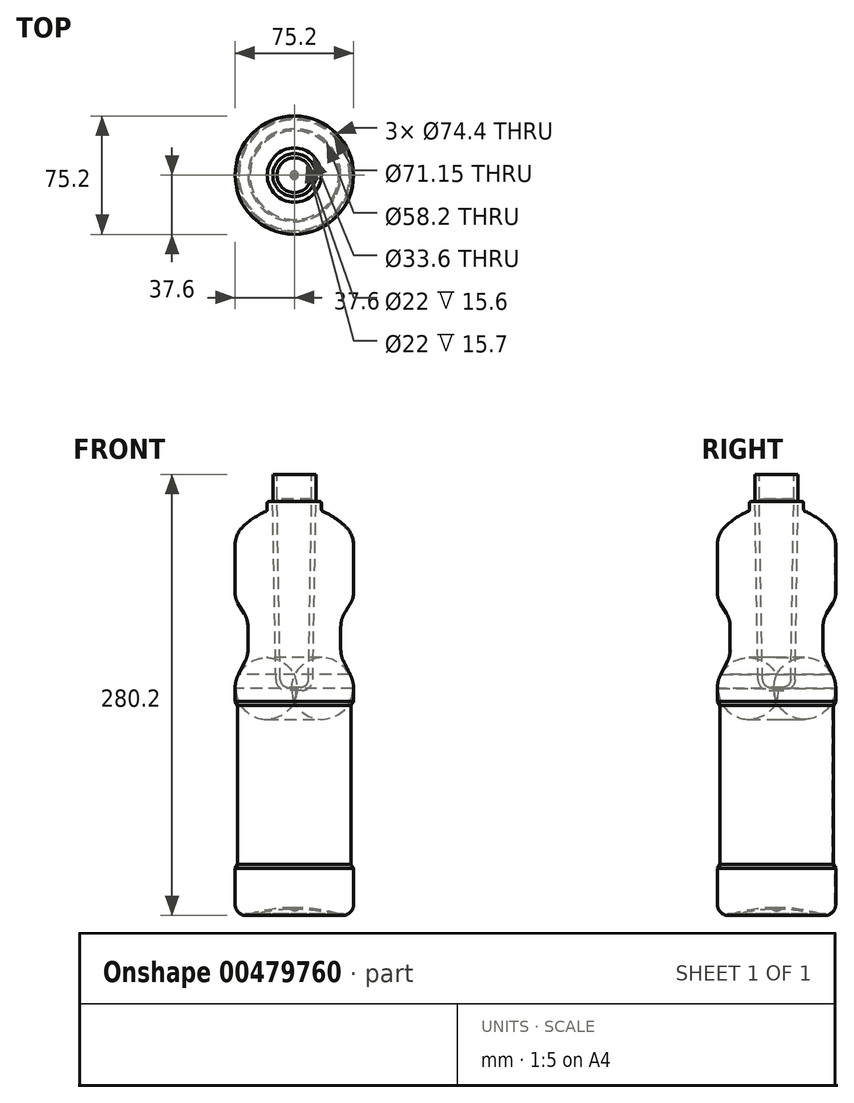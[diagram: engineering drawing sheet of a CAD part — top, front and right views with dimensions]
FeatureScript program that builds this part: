
annotation { "Feature Type Name" : "Feature", "Feature Type Description" : "" }
export const myFeature = defineFeature(function(context is Context, id is Id, definition is map)
    precondition{}
    {
        {
            var Q0;
            Q0=qCreatedBy(makeId("Front.planeOp"),FACE);
            var sketch = newSketch(context, id + "F0", { "sketchPlane" : qUnion([Q0])});
            skLineSegment(sketch, "E0", {"start": v(7.8, 140.1) * mm, "end": v(5.15, 140.1) * mm});
            skLineSegment(sketch, "E1", {"start": v(-11.8, -140.1) * mm, "end": v(-9.3, -140.1) * mm});
            skArc(sketch, "E2", {"start": v(16.2, -136.13) * mm, "mid": v(3.32, -137.3) * mm, "end": v(-9.3, -140.1) * mm});
            skLineSegment(sketch, "E3", {"start": v(-18.8, -133.1) * mm, "end": v(-18.8, -110.1) * mm});
            skArc(sketch, "E4", {"start": v(-18.8, -133.1) * mm, "mid": v(-16.75, -138.05) * mm, "end": v(-11.8, -140.1) * mm});
            skLineSegment(sketch, "E5", {"start": v(-17.18, -107.6) * mm, "end": v(-18.8, -110.1) * mm});
            skLineSegment(sketch, "E6", {"start": v(-17.18, -6.6) * mm, "end": v(-17.18, -107.6) * mm});
            skLineSegment(sketch, "E7", {"start": v(-17.18, -6.6) * mm, "end": v(-18.8, -4.1) * mm});
            skLineSegment(sketch, "E8", {"start": v(-16.64, 13.16) * mm, "end": v(-12.43, 21.5) * mm});
            skLineSegment(sketch, "E9", {"start": v(-10.7, 28.72) * mm, "end": v(-10.7, 43.47) * mm});
            skLineSegment(sketch, "E10", {"start": v(-12.98, 51.7) * mm, "end": v(-17.09, 58.55) * mm});
            skArc(sketch, "E11", {"start": v(-16.64, 13.16) * mm, "mid": v(-18.25, 8.77) * mm, "end": v(-18.8, 4.13) * mm});
            skArc(sketch, "E12", {"start": v(-12.43, 21.5) * mm, "mid": v(-11.14, 25) * mm, "end": v(-10.7, 28.72) * mm});
            skArc(sketch, "E13", {"start": v(-10.7, 43.47) * mm, "mid": v(-11.28, 47.74) * mm, "end": v(-12.98, 51.7) * mm});
            skLineSegment(sketch, "E14", {"start": v(-18.8, 64.72) * mm, "end": v(-18.8, 95.32) * mm});
            skArc(sketch, "E15", {"start": v(-18.8, 64.72) * mm, "mid": v(-18.36, 61.52) * mm, "end": v(-17.09, 58.55) * mm});
            skArc(sketch, "E16", {"start": v(-14.11, 106.63) * mm, "mid": v(-17.58, 101.44) * mm, "end": v(-18.8, 95.32) * mm});
            skArc(sketch, "E17", {"start": v(0.68, 116.6) * mm, "mid": v(-7.2, 112.33) * mm, "end": v(-14.11, 106.63) * mm});
            skLineSegment(sketch, "E18", {"start": v(-18.8, -4.1) * mm, "end": v(-18.8, 4.13) * mm});
            skLineSegment(sketch, "E19", {"start": v(5.15, 123.9) * mm, "end": v(5.15, 140.1) * mm});
            skLineSegment(sketch, "E20", {"start": v(1.6, 117.98) * mm, "end": v(1.6, 121.9) * mm});
            skLineSegment(sketch, "E21", {"start": v(2.6, 122.9) * mm, "end": v(4.15, 122.9) * mm});
            skLineSegment(sketch, "E22", {"start": v(7.8, 140.1) * mm, "end": v(7.8, 124.4) * mm});
            skArc(sketch, "E23", {"start": v(2.6, 122.9) * mm, "mid": v(1.9, 122.6) * mm, "end": v(1.6, 121.9) * mm});
            skArc(sketch, "E24", {"start": v(4.15, 122.9) * mm, "mid": v(4.85, 123.2) * mm, "end": v(5.15, 123.9) * mm});
            skArc(sketch, "E25", {"start": v(0.68, 116.6) * mm, "mid": v(1.35, 117.15) * mm, "end": v(1.6, 117.98) * mm});
            skArc(sketch, "E26", {"start": v(0.88, 116.13) * mm, "mid": v(-6.92, 111.91) * mm, "end": v(-13.76, 106.28) * mm});
            skArc(sketch, "E27", {"start": v(-13.76, 106.28) * mm, "mid": v(-17.12, 101.25) * mm, "end": v(-18.3, 95.32) * mm});
            skLineSegment(sketch, "E28", {"start": v(-18.3, 64.72) * mm, "end": v(-18.3, 95.32) * mm});
            skArc(sketch, "E29", {"start": v(-18.3, 64.72) * mm, "mid": v(-17.88, 61.65) * mm, "end": v(-16.66, 58.8) * mm});
            skLineSegment(sketch, "E30", {"start": v(-12.55, 51.96) * mm, "end": v(-16.66, 58.8) * mm});
            skArc(sketch, "E31", {"start": v(-10.2, 43.47) * mm, "mid": v(-10.8, 47.87) * mm, "end": v(-12.55, 51.96) * mm});
            skLineSegment(sketch, "E32", {"start": v(-10.2, 28.72) * mm, "end": v(-10.2, 43.47) * mm});
            skArc(sketch, "E33", {"start": v(-11.98, 21.27) * mm, "mid": v(-10.65, 24.89) * mm, "end": v(-10.2, 28.72) * mm});
            skLineSegment(sketch, "E34", {"start": v(-16.2, 12.93) * mm, "end": v(-11.98, 21.27) * mm});
            skArc(sketch, "E35", {"start": v(-16.2, 12.93) * mm, "mid": v(-17.77, 8.65) * mm, "end": v(-18.3, 4.13) * mm});
            skLineSegment(sketch, "E36", {"start": v(-18.3, -3.95) * mm, "end": v(-18.3, 4.13) * mm});
            skLineSegment(sketch, "E37", {"start": v(-16.68, -6.45) * mm, "end": v(-18.3, -3.95) * mm});
            skLineSegment(sketch, "E38", {"start": v(-16.68, -6.45) * mm, "end": v(-16.68, -107.75) * mm});
            skLineSegment(sketch, "E39", {"start": v(-16.68, -107.75) * mm, "end": v(-18.3, -110.25) * mm});
            skLineSegment(sketch, "E40", {"start": v(-18.3, -133.1) * mm, "end": v(-18.3, -110.25) * mm});
            skArc(sketch, "E41", {"start": v(-18.3, -133.1) * mm, "mid": v(-16.4, -137.7) * mm, "end": v(-11.8, -139.6) * mm});
            skLineSegment(sketch, "E42", {"start": v(-11.8, -139.6) * mm, "end": v(-9.37, -139.6) * mm});
            skArc(sketch, "E43", {"start": v(18.8, -135.6) * mm, "mid": v(4.57, -136.6) * mm, "end": v(-9.37, -139.6) * mm});
            skArc(sketch, "E44", {"start": v(0.88, 116.13) * mm, "mid": v(1.77, 116.87) * mm, "end": v(2.1, 117.98) * mm});
            skLineSegment(sketch, "E45", {"start": v(2.1, 117.98) * mm, "end": v(2.1, 121.9) * mm});
            skArc(sketch, "E46", {"start": v(2.6, 122.4) * mm, "mid": v(2.25, 122.25) * mm, "end": v(2.1, 121.9) * mm});
            skLineSegment(sketch, "E47", {"start": v(2.6, 122.4) * mm, "end": v(5.8, 122.4) * mm});
            skArc(sketch, "E48", {"start": v(5.8, 122.4) * mm, "mid": v(7.21, 122.99) * mm, "end": v(7.8, 124.4) * mm});
            skArc(sketch, "E49", {"start": v(16.2, -136.13) * mm, "mid": v(17.4, -136.85) * mm, "end": v(18.8, -137.1) * mm});
            skLineSegment(sketch, "E50", {"start": v(18.8, -135.6) * mm, "end": v(18.8, -137.1) * mm});
            skSolve(sketch);
        }
        {
            var Q0;
            Q0=qCreatedBy(makeId("Front.planeOp"),FACE);
            var sketch = newSketch(context, id + "F1", { "sketchPlane" : qUnion([Q0])});
            skPoint(sketch, "E51.0", {"position": v(18.8, -137.1) * mm});
            skPoint(sketch, "E52.0", {"position": v(18.8, -133.1) * mm});
            skLineSegment(sketch, "E53", {"start": v(18.8, -133.1) * mm, "end": v(18.8, -137.1) * mm});
            skSolve(sketch);
        }
        {
            var Q0;
            Q0=qCreatedBy(makeId("Front.planeOp"),FACE);
            var sketch = newSketch(context, id + "F2", { "sketchPlane" : qUnion([Q0])});
            skLineSegment(sketch, "E54.0", {"start": v(7.8, 140.1) * mm, "end": v(5.15, 140.1) * mm});
            skLineSegment(sketch, "E55.0", {"start": v(7.8, 140.1) * mm, "end": v(7.8, 124.5) * mm});
            skLineSegment(sketch, "E56.0", {"start": v(5.15, 123.9) * mm, "end": v(5.15, 140.1) * mm});
            skArc(sketch, "E57.0", {"start": v(4.15, 122.9) * mm, "mid": v(4.85, 123.2) * mm, "end": v(5.15, 123.9) * mm});
            skLineSegment(sketch, "E58.0", {"start": v(2.6, 122.9) * mm, "end": v(4.15, 122.9) * mm});
            skArc(sketch, "E59.0", {"start": v(2.6, 122.9) * mm, "mid": v(1.9, 122.6) * mm, "end": v(1.6, 121.9) * mm});
            skLineSegment(sketch, "E60.0", {"start": v(1.6, 117.98) * mm, "end": v(1.6, 121.9) * mm});
            skArc(sketch, "E61.0", {"start": v(0.68, 116.6) * mm, "mid": v(1.35, 117.15) * mm, "end": v(1.6, 117.98) * mm});
            skArc(sketch, "E62.0", {"start": v(0.68, 116.6) * mm, "mid": v(-7.2, 112.33) * mm, "end": v(-14.11, 106.63) * mm});
            skArc(sketch, "E63.0", {"start": v(-14.11, 106.63) * mm, "mid": v(-17.58, 101.44) * mm, "end": v(-18.8, 95.32) * mm});
            skLineSegment(sketch, "E64.0", {"start": v(-18.8, 64.72) * mm, "end": v(-18.8, 95.32) * mm});
            skArc(sketch, "E65.0", {"start": v(-18.8, 64.72) * mm, "mid": v(-18.36, 61.52) * mm, "end": v(-17.09, 58.55) * mm});
            skLineSegment(sketch, "E66.0", {"start": v(-12.98, 51.7) * mm, "end": v(-17.09, 58.55) * mm});
            skArc(sketch, "E67.0", {"start": v(-10.7, 43.47) * mm, "mid": v(-11.28, 47.74) * mm, "end": v(-12.98, 51.7) * mm});
            skLineSegment(sketch, "E68.0", {"start": v(-10.7, 28.72) * mm, "end": v(-10.7, 43.47) * mm});
            skArc(sketch, "E69.0", {"start": v(-12.43, 21.5) * mm, "mid": v(-11.14, 25) * mm, "end": v(-10.7, 28.72) * mm});
            skLineSegment(sketch, "E70.0", {"start": v(-16.64, 13.16) * mm, "end": v(-12.43, 21.5) * mm});
            skArc(sketch, "E71.0", {"start": v(-16.64, 13.16) * mm, "mid": v(-18.25, 8.77) * mm, "end": v(-18.8, 4.13) * mm});
            skLineSegment(sketch, "E72.0", {"start": v(-18.8, -4.1) * mm, "end": v(-18.8, 4.13) * mm});
            skLineSegment(sketch, "E73.0", {"start": v(-17.18, -6.6) * mm, "end": v(-18.8, -4.1) * mm});
            skLineSegment(sketch, "E74.0", {"start": v(-17.18, -6.6) * mm, "end": v(-17.18, -107.6) * mm});
            skLineSegment(sketch, "E75.0", {"start": v(-17.18, -107.6) * mm, "end": v(-18.8, -110.1) * mm});
            skLineSegment(sketch, "E76.0", {"start": v(-18.8, -133.1) * mm, "end": v(-18.8, -110.1) * mm});
            skArc(sketch, "E77.0", {"start": v(-18.8, -133.1) * mm, "mid": v(-16.75, -138.05) * mm, "end": v(-11.8, -140.1) * mm});
            skLineSegment(sketch, "E78.0", {"start": v(-11.8, -140.1) * mm, "end": v(-9.3, -140.1) * mm});
            skArc(sketch, "E79.0", {"start": v(16.2, -136.13) * mm, "mid": v(3.32, -137.3) * mm, "end": v(-9.3, -140.1) * mm});
            skArc(sketch, "E80.0", {"start": v(16.2, -136.13) * mm, "mid": v(17.4, -136.85) * mm, "end": v(18.8, -137.1) * mm});
            skLineSegment(sketch, "E81.0", {"start": v(18.8, -133.1) * mm, "end": v(18.8, -137.1) * mm});
            skArc(sketch, "E82.0", {"start": v(18.8, -135.1) * mm, "mid": v(4.54, -136.1) * mm, "end": v(-9.44, -139.1) * mm});
            skLineSegment(sketch, "E83.0", {"start": v(-18.4, -133.1) * mm, "end": v(-18.4, -110.22) * mm});
            skLineSegment(sketch, "E84.0", {"start": v(-16.78, -107.72) * mm, "end": v(-18.4, -110.22) * mm});
            skLineSegment(sketch, "E85.0", {"start": v(-16.78, -6.48) * mm, "end": v(-16.78, -107.72) * mm});
            skLineSegment(sketch, "E86.0", {"start": v(-16.78, -6.48) * mm, "end": v(-18.4, -3.98) * mm});
            skLineSegment(sketch, "E87.0", {"start": v(-18.4, -3.98) * mm, "end": v(-18.4, 4.13) * mm});
            skArc(sketch, "E88.0", {"start": v(-16.29, 12.98) * mm, "mid": v(-17.86, 8.68) * mm, "end": v(-18.4, 4.13) * mm});
            skLineSegment(sketch, "E89.0", {"start": v(-16.29, 12.98) * mm, "end": v(-12.07, 21.31) * mm});
            skArc(sketch, "E90.0", {"start": v(-12.07, 21.31) * mm, "mid": v(-10.75, 24.91) * mm, "end": v(-10.3, 28.72) * mm});
            skLineSegment(sketch, "E91.0", {"start": v(-10.3, 28.72) * mm, "end": v(-10.3, 43.47) * mm});
            skArc(sketch, "E92.0", {"start": v(-10.3, 43.47) * mm, "mid": v(-10.9, 47.85) * mm, "end": v(-12.64, 51.9) * mm});
            skLineSegment(sketch, "E93.0", {"start": v(-12.64, 51.9) * mm, "end": v(-16.75, 58.76) * mm});
            skArc(sketch, "E94.0", {"start": v(-18.4, 64.72) * mm, "mid": v(-17.98, 61.63) * mm, "end": v(-16.75, 58.76) * mm});
            skLineSegment(sketch, "E95.0", {"start": v(-18.4, 64.72) * mm, "end": v(-18.4, 95.32) * mm});
            skArc(sketch, "E96.0", {"start": v(-13.83, 106.35) * mm, "mid": v(-17.21, 101.29) * mm, "end": v(-18.4, 95.32) * mm});
            skArc(sketch, "E97.0", {"start": v(0.84, 116.23) * mm, "mid": v(-6.97, 112) * mm, "end": v(-13.83, 106.35) * mm});
            skArc(sketch, "E98.0", {"start": v(0.84, 116.23) * mm, "mid": v(1.68, 116.93) * mm, "end": v(2, 117.98) * mm});
            skLineSegment(sketch, "E99.0", {"start": v(2, 117.98) * mm, "end": v(2, 121.9) * mm});
            skArc(sketch, "E100.0", {"start": v(2.6, 122.5) * mm, "mid": v(2.18, 122.32) * mm, "end": v(2, 121.9) * mm});
            skLineSegment(sketch, "E101.0", {"start": v(2.6, 122.5) * mm, "end": v(5.8, 122.5) * mm});
            skPoint(sketch, "E102.newPointB", {"position": v(7.8, 124.4) * mm});
            skArc(sketch, "E102.filletArc", {"start": v(5.8, 122.5) * mm, "mid": v(7.21, 123.09) * mm, "end": v(7.8, 124.5) * mm});
            skLineSegment(sketch, "E103.0", {"start": v(-12.4, -139.1) * mm, "end": v(-9.44, -139.1) * mm});
            skArc(sketch, "E104", {"start": v(-18.4, -133.1) * mm, "mid": v(-16.64, -137.34) * mm, "end": v(-12.4, -139.1) * mm});
            skSolve(sketch);
        }
        {
            var Q0;
            Q0 = qSketchRegion(id + "F2", true);
            var Q1;
            Q1=sQuery(id+"F1.wireOp",EDGE,"E53");
            revolve(context, id + "F3", {"entities" : qUnion([Q0]), "axis" : qUnion([Q1]), "revolveType" : RevolveType.FULL});
        }
        {
            var Q0;
            Q0=qCreatedBy(makeId("Front.planeOp"),FACE);
            var sketch = newSketch(context, id + "F4", { "sketchPlane" : qUnion([Q0])});
            skLineSegment(sketch, "E105.0", {"start": v(7.8, 140.1) * mm, "end": v(5.15, 140.1) * mm});
            skLineSegment(sketch, "E106.0", {"start": v(5.15, 122.9) * mm, "end": v(5.15, 140.1) * mm});
            skLineSegment(sketch, "E107.0", {"start": v(7.8, 140.1) * mm, "end": v(7.8, 124.4) * mm});
            skLineSegment(sketch, "E108", {"start": v(7.8, 124.4) * mm, "end": v(9.89, 4.9) * mm});
            skPoint(sketch, "E109.0", {"position": v(18.8, -136.35) * mm});
            skPoint(sketch, "E110.0", {"position": v(18.8, -135.6) * mm});
            skLineSegment(sketch, "E111", {"start": v(18.8, -136.35) * mm, "end": v(18.8, 140.1) * mm});
            skLineSegment(sketch, "E112", {"start": v(7.8, 140.1) * mm, "end": v(65.63, 140.1) * mm});
            skLineSegment(sketch, "E113", {"start": v(18.8, -2.1) * mm, "end": v(18, -2.1) * mm});
            skLineSegment(sketch, "E114", {"start": v(18, -2.1) * mm, "end": v(17.56, 2.9) * mm});
            skPoint(sketch, "E115.orphan", {"position": v(4.15, 122.9) * mm});
            skPoint(sketch, "E116.orphan", {"position": v(5.15, 123.9) * mm});
            skLineSegment(sketch, "E117", {"start": v(5.07, 123.5) * mm, "end": v(7.17, 2.9) * mm});
            skLineSegment(sketch, "E118", {"start": v(7.17, 2.9) * mm, "end": v(17.56, 2.9) * mm});
            skLineSegment(sketch, "E119", {"start": v(9.89, 4.9) * mm, "end": v(18.8, 4.9) * mm});
            skLineSegment(sketch, "E120.trimOffspring", {"start": v(3.37, 122.9) * mm, "end": v(5.15, 122.9) * mm});
            skPoint(sketch, "E121.0.start.orphan", {"position": v(2.6, 122.9) * mm});
            skLineSegment(sketch, "E122.0", {"start": v(2.6, 122.9) * mm, "end": v(4.15, 122.9) * mm});
            skLineSegment(sketch, "E123.0.0", {"start": v(-18.8, -4.1) * mm, "end": v(-17.18, -6.6) * mm, "construction": true});
            skLineSegment(sketch, "E123.0.1", {"start": v(-17.18, -6.6) * mm, "end": v(-17.18, -107.6) * mm, "construction": true});
            skLineSegment(sketch, "E123.0.2", {"start": v(-17.18, -107.6) * mm, "end": v(-18.8, -110.1) * mm, "construction": true});
            skLineSegment(sketch, "E123.0.3", {"start": v(-18.8, -110.1) * mm, "end": v(-18.8, -133.1) * mm, "construction": true});
            skArc(sketch, "E123.0.4", {"start": v(-18.8, -133.1) * mm, "mid": v(-16.75, -138.05) * mm, "end": v(-11.8, -140.1) * mm, "construction": true});
            skLineSegment(sketch, "E123.0.5", {"start": v(-11.8, -140.1) * mm, "end": v(-9.3, -140.1) * mm, "construction": true});
            skArc(sketch, "E123.0.6", {"start": v(-9.3, -140.1) * mm, "mid": v(3.32, -137.3) * mm, "end": v(16.2, -136.13) * mm, "construction": true});
            skArc(sketch, "E123.0.7", {"start": v(16.2, -136.13) * mm, "mid": v(17.4, -136.85) * mm, "end": v(18.8, -137.1) * mm, "construction": true});
            skLineSegment(sketch, "E123.0.8", {"start": v(18.8, -137.1) * mm, "end": v(18.8, -135.6) * mm, "construction": true});
            skArc(sketch, "E123.0.9", {"start": v(18.8, -135.6) * mm, "mid": v(4.57, -136.6) * mm, "end": v(-9.37, -139.6) * mm, "construction": true});
            skLineSegment(sketch, "E123.0.10", {"start": v(-9.37, -139.6) * mm, "end": v(-11.8, -139.6) * mm, "construction": true});
            skArc(sketch, "E123.0.11", {"start": v(-11.8, -139.6) * mm, "mid": v(-16.4, -137.7) * mm, "end": v(-18.3, -133.1) * mm, "construction": true});
            skLineSegment(sketch, "E123.0.12", {"start": v(-18.3, -133.1) * mm, "end": v(-18.3, -110.25) * mm, "construction": true});
            skLineSegment(sketch, "E123.0.13", {"start": v(-18.3, -110.25) * mm, "end": v(-16.68, -107.75) * mm, "construction": true});
            skLineSegment(sketch, "E123.0.14", {"start": v(-16.68, -107.75) * mm, "end": v(-16.68, -6.45) * mm, "construction": true});
            skLineSegment(sketch, "E123.0.15", {"start": v(-16.68, -6.45) * mm, "end": v(-18.3, -3.95) * mm, "construction": true});
            skLineSegment(sketch, "E123.0.16", {"start": v(-18.3, -3.95) * mm, "end": v(-18.3, 4.13) * mm, "construction": true});
            skArc(sketch, "E123.0.17", {"start": v(-18.3, 4.13) * mm, "mid": v(-17.77, 8.65) * mm, "end": v(-16.2, 12.93) * mm, "construction": true});
            skLineSegment(sketch, "E123.0.18", {"start": v(-16.2, 12.93) * mm, "end": v(-11.98, 21.27) * mm, "construction": true});
            skArc(sketch, "E123.0.19", {"start": v(-11.98, 21.27) * mm, "mid": v(-10.65, 24.89) * mm, "end": v(-10.2, 28.72) * mm, "construction": true});
            skLineSegment(sketch, "E123.0.20", {"start": v(-10.2, 28.72) * mm, "end": v(-10.2, 43.47) * mm, "construction": true});
            skArc(sketch, "E123.0.21", {"start": v(-10.2, 43.47) * mm, "mid": v(-10.8, 47.87) * mm, "end": v(-12.55, 51.96) * mm, "construction": true});
            skLineSegment(sketch, "E123.0.22", {"start": v(-12.55, 51.96) * mm, "end": v(-16.66, 58.8) * mm, "construction": true});
            skArc(sketch, "E123.0.23", {"start": v(-16.66, 58.8) * mm, "mid": v(-17.88, 61.65) * mm, "end": v(-18.3, 64.72) * mm, "construction": true});
            skLineSegment(sketch, "E123.0.24", {"start": v(-18.3, 64.72) * mm, "end": v(-18.3, 95.32) * mm, "construction": true});
            skArc(sketch, "E123.0.25", {"start": v(-18.3, 95.32) * mm, "mid": v(-17.12, 101.25) * mm, "end": v(-13.76, 106.28) * mm, "construction": true});
            skArc(sketch, "E123.0.26", {"start": v(-13.76, 106.28) * mm, "mid": v(-6.92, 111.91) * mm, "end": v(0.88, 116.13) * mm, "construction": true});
            skArc(sketch, "E123.0.27", {"start": v(0.88, 116.13) * mm, "mid": v(1.77, 116.87) * mm, "end": v(2.1, 117.98) * mm, "construction": true});
            skLineSegment(sketch, "E123.0.28", {"start": v(2.1, 117.98) * mm, "end": v(2.1, 121.9) * mm, "construction": true});
            skArc(sketch, "E123.0.29", {"start": v(2.1, 121.9) * mm, "mid": v(2.25, 122.25) * mm, "end": v(2.6, 122.4) * mm, "construction": true});
            skLineSegment(sketch, "E123.0.30", {"start": v(2.6, 122.4) * mm, "end": v(5.8, 122.4) * mm, "construction": true});
            skArc(sketch, "E123.0.31", {"start": v(5.8, 122.4) * mm, "mid": v(7.21, 122.99) * mm, "end": v(7.8, 124.4) * mm, "construction": true});
            skLineSegment(sketch, "E123.0.32", {"start": v(7.8, 124.4) * mm, "end": v(7.8, 140.1) * mm, "construction": true});
            skLineSegment(sketch, "E123.0.33", {"start": v(7.8, 140.1) * mm, "end": v(5.15, 140.1) * mm, "construction": true});
            skLineSegment(sketch, "E123.0.34", {"start": v(5.15, 140.1) * mm, "end": v(5.15, 123.9) * mm, "construction": true});
            skArc(sketch, "E123.0.35", {"start": v(5.15, 123.9) * mm, "mid": v(4.85, 123.2) * mm, "end": v(4.15, 122.9) * mm, "construction": true});
            skLineSegment(sketch, "E123.0.36", {"start": v(4.15, 122.9) * mm, "end": v(2.6, 122.9) * mm, "construction": true});
            skArc(sketch, "E123.0.37", {"start": v(2.6, 122.9) * mm, "mid": v(1.9, 122.6) * mm, "end": v(1.6, 121.9) * mm, "construction": true});
            skLineSegment(sketch, "E123.0.38", {"start": v(1.6, 121.9) * mm, "end": v(1.6, 117.98) * mm, "construction": true});
            skArc(sketch, "E123.0.39", {"start": v(1.6, 117.98) * mm, "mid": v(1.35, 117.15) * mm, "end": v(0.68, 116.6) * mm, "construction": true});
            skArc(sketch, "E123.0.40", {"start": v(0.68, 116.6) * mm, "mid": v(-7.2, 112.33) * mm, "end": v(-14.11, 106.63) * mm, "construction": true});
            skArc(sketch, "E123.0.41", {"start": v(-14.11, 106.63) * mm, "mid": v(-17.58, 101.44) * mm, "end": v(-18.8, 95.32) * mm, "construction": true});
            skLineSegment(sketch, "E123.0.42", {"start": v(-18.8, 95.32) * mm, "end": v(-18.8, 64.72) * mm, "construction": true});
            skArc(sketch, "E123.0.43", {"start": v(-18.8, 64.72) * mm, "mid": v(-18.36, 61.52) * mm, "end": v(-17.09, 58.55) * mm, "construction": true});
            skLineSegment(sketch, "E123.0.44", {"start": v(-17.09, 58.55) * mm, "end": v(-12.98, 51.7) * mm, "construction": true});
            skArc(sketch, "E123.0.45", {"start": v(-12.98, 51.7) * mm, "mid": v(-11.28, 47.74) * mm, "end": v(-10.7, 43.47) * mm, "construction": true});
            skLineSegment(sketch, "E123.0.46", {"start": v(-10.7, 43.47) * mm, "end": v(-10.7, 28.72) * mm, "construction": true});
            skArc(sketch, "E123.0.47", {"start": v(-10.7, 28.72) * mm, "mid": v(-11.14, 25) * mm, "end": v(-12.43, 21.5) * mm, "construction": true});
            skLineSegment(sketch, "E123.0.48", {"start": v(-12.43, 21.5) * mm, "end": v(-16.64, 13.16) * mm, "construction": true});
            skArc(sketch, "E123.0.49", {"start": v(-16.64, 13.16) * mm, "mid": v(-18.25, 8.77) * mm, "end": v(-18.8, 4.13) * mm, "construction": true});
            skLineSegment(sketch, "E123.0.50", {"start": v(-18.8, 4.13) * mm, "end": v(-18.8, -4.1) * mm, "construction": true});
            skPoint(sketch, "E124.orphan", {"position": v(5.03, 125.34) * mm});
            skSolve(sketch);
        }
        {
            var Q0;
            Q0=qCreatedBy(makeId("Front.planeOp"),FACE);
            var sketch = newSketch(context, id + "F5", { "sketchPlane" : qUnion([Q0])});
            skLineSegment(sketch, "E125.0", {"start": v(7.8, 140.1) * mm, "end": v(5.15, 140.1) * mm});
            skLineSegment(sketch, "E126.0", {"start": v(7.8, 140.1) * mm, "end": v(7.8, 124.4) * mm});
            skLineSegment(sketch, "E127.0", {"start": v(5.15, 122.9) * mm, "end": v(5.15, 140.1) * mm});
            skLineSegment(sketch, "E128.0", {"start": v(5.08, 122.9) * mm, "end": v(7.05, 9.78) * mm});
            skLineSegment(sketch, "E129.0", {"start": v(5.08, 122.9) * mm, "end": v(5.15, 122.9) * mm});
            skLineSegment(sketch, "E130.0", {"start": v(7.8, 124.4) * mm, "end": v(9.8, 9.81) * mm});
            skLineSegment(sketch, "E131.0", {"start": v(14.8, 4.9) * mm, "end": v(18.8, 4.9) * mm});
            skLineSegment(sketch, "E132.0", {"start": v(14.05, 2.9) * mm, "end": v(17.56, 2.9) * mm});
            skLineSegment(sketch, "E133.0", {"start": v(18, -2.1) * mm, "end": v(17.56, 2.9) * mm});
            skLineSegment(sketch, "E134.0", {"start": v(18.8, -2.1) * mm, "end": v(18, -2.1) * mm});
            skLineSegment(sketch, "E135", {"start": v(18.8, 4.9) * mm, "end": v(18.8, -2.1) * mm});
            skPoint(sketch, "E136.visualSharp", {"position": v(9.89, 4.9) * mm});
            skArc(sketch, "E136.filletArc", {"start": v(9.8, 9.81) * mm, "mid": v(11.3, 6.33) * mm, "end": v(14.8, 4.9) * mm});
            skPoint(sketch, "E137.visualSharp", {"position": v(7.17, 2.9) * mm});
            skArc(sketch, "E137.filletArc", {"start": v(7.05, 9.78) * mm, "mid": v(9.14, 4.9) * mm, "end": v(14.05, 2.9) * mm});
            skPoint(sketch, "E138.orphan", {"position": v(5.07, 123.5) * mm});
            skPoint(sketch, "E139.orphan", {"position": v(3.37, 122.9) * mm});
            skSolve(sketch);
        }
        {
            var Q0;
            Q0=makeQuery(id+"F5.imprint","IMPRINT",FACE,{"disambiguationData":[TD([[makeQuery(id+"F5.imprint","IMPRINT",EDGE,{"derivedFrom":sQuery(id+"F5.wireOp",EDGE,"E125.0")}),1.0]])]});
            var Q1;
            Q1=sQuery(id+"F5.wireOp",EDGE,"E135");
            revolve(context, id + "F6", {"entities" : qUnion([Q0]), "axis" : qUnion([Q1]), "revolveType" : RevolveType.FULL});
        }
    });
